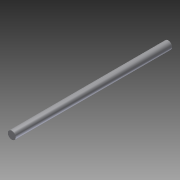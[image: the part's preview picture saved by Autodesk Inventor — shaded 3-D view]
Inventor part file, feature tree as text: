
AUTODESK INVENTOR PART (.ipt)
format: ipt  version: 2012 (Build 160160000, 160)  size: 65,536 bytes
history: native  units: in
note: dims shown in document units (in); Inventor stores cm internally (conversion verified against a paired STEP export)
features: extrude x1, sketch x1
ambient origin geometry x8: Origin, YZ Plane, XZ Plane, XY Plane, X Axis, Y Axis, Z Axis, Center Point
bodies: Solid1 (feature_tree)
feature tree (2):
  extrude  "Extrusion1"  Depth=10.0in TaperAngle=0.0deg
  sketch  "Sketch1"  dims[d0=0.5in d1=10.0in d2=0.0in]
